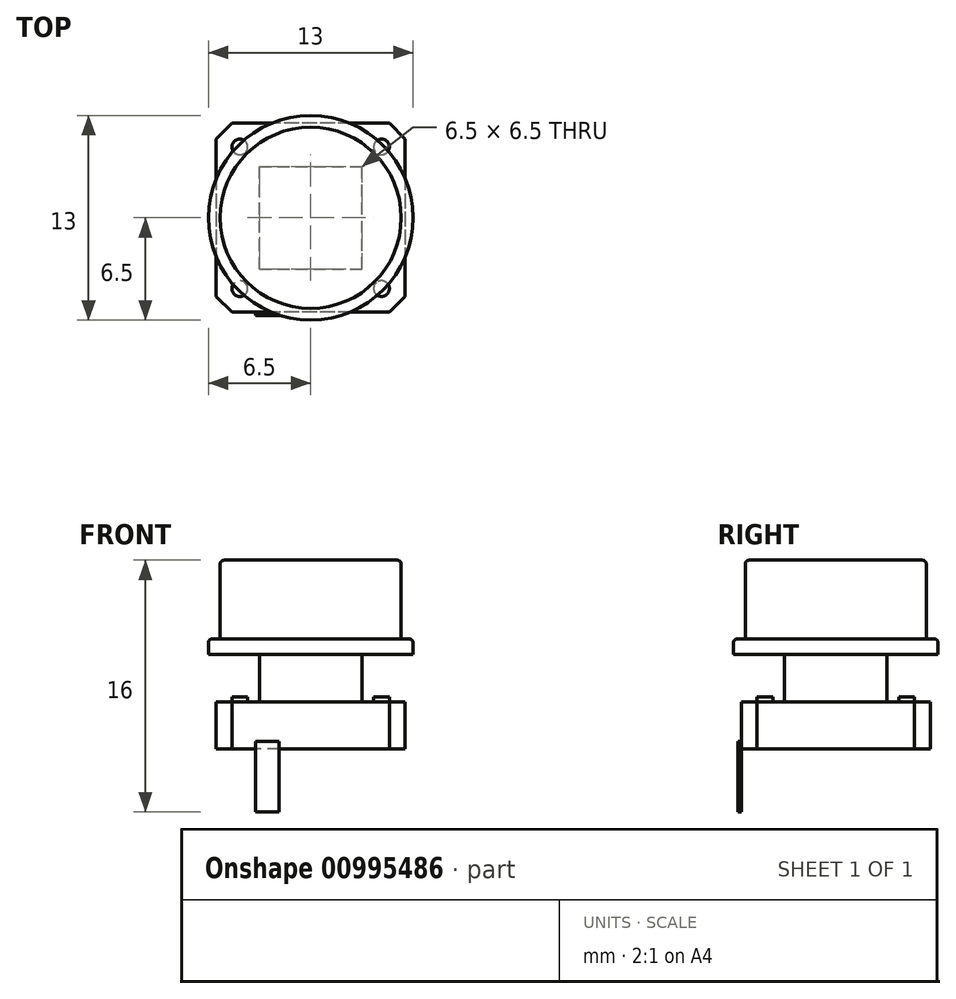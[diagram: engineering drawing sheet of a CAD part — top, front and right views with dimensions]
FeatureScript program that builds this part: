
annotation { "Feature Type Name" : "Feature", "Feature Type Description" : "" }
export const myFeature = defineFeature(function(context is Context, id is Id, definition is map)
    precondition{}
    {
        {
            var Q0;
            Q0=qCreatedBy(makeId("Top.planeOp"),FACE);
            var sketch = newSketch(context, id + "F0", { "sketchPlane" : qUnion([Q0])});
            skLineSegment(sketch, "E0.bottom", {"start": v(6, 6) * mm, "end": v(-6, 6) * mm});
            skLineSegment(sketch, "E0.top", {"start": v(6, -6) * mm, "end": v(-6, -6) * mm});
            skLineSegment(sketch, "E0.left", {"start": v(6, 6) * mm, "end": v(6, -6) * mm});
            skLineSegment(sketch, "E0.right", {"start": v(-6, 6) * mm, "end": v(-6, -6) * mm});
            skPoint(sketch, "E0.middle", {"position": v(0, 0) * mm});
            skCircle(sketch, "E1", {"center": v(0, 0) * mm, "radius": 5.75 * mm});
            skCircle(sketch, "E2", {"center": v(0, 0) * mm, "radius": 6.5 * mm});
            skLineSegment(sketch, "E3.bottom", {"start": v(3.25, 3.25) * mm, "end": v(-3.25, 3.25) * mm});
            skLineSegment(sketch, "E3.top", {"start": v(3.25, -3.25) * mm, "end": v(-3.25, -3.25) * mm});
            skLineSegment(sketch, "E3.left", {"start": v(3.25, 3.25) * mm, "end": v(3.25, -3.25) * mm});
            skLineSegment(sketch, "E3.right", {"start": v(-3.25, 3.25) * mm, "end": v(-3.25, -3.25) * mm});
            skLineSegment(sketch, "E4", {"start": v(6, -6) * mm, "end": v(4.5, -6) * mm});
            skLineSegment(sketch, "E5", {"start": v(4.5, -6) * mm, "end": v(4.5, -4.5) * mm});
            skCircle(sketch, "E6", {"center": v(4.5, -4.5) * mm, "radius": 0.5 * mm});
            skCircle(sketch, "E7.MirrorC", {"center": v(-4.5, -4.5) * mm, "radius": 0.5 * mm});
            skCircle(sketch, "E8.MirrorC", {"center": v(-4.5, 4.5) * mm, "radius": 0.5 * mm});
            skCircle(sketch, "E9.MirrorC", {"center": v(4.5, 4.5) * mm, "radius": 0.5 * mm});
            skSolve(sketch);
        }
        {
            var Q0;
            {var subQ0=sQuery(id+"F0.wireOp",EDGE,"E0.right");var subQ1=sQuery(id+"F0.wireOp",EDGE,"E0.bottom");var subQ2=makeQuery(id+"F0.imprint","INTERSECT",VERTEX,{"derivedFrom":[subQ1,subQ0]});Q0=makeQuery(id+"F0.imprint","IMPRINT",FACE,{"disambiguationData":[TD([[makeQuery(id+"F0.imprint","IMPRINT",EDGE,{"disambiguationData":[TD([[subQ2,1.0]])],"derivedFrom":subQ1}),1.0]])]});}
            var Q1;
            Q1=makeQuery(id+"F0.imprint","IMPRINT",FACE,{"disambiguationData":[TD([[makeQuery(id+"F0.imprint","IMPRINT",EDGE,{"derivedFrom":sQuery(id+"F0.wireOp",EDGE,"E1")}),1.0]])]});
            var Q2;
            Q2=makeQuery(id+"F0.imprint","IMPRINT",FACE,{"disambiguationData":[TD([[makeQuery(id+"F0.imprint","IMPRINT",EDGE,{"derivedFrom":sQuery(id+"F0.wireOp",EDGE,"E3.bottom")}),1.0]])]});
            var Q3;
            {var subQ0=sQuery(id+"F0.wireOp",EDGE,"E0.left");var subQ1=sQuery(id+"F0.wireOp",EDGE,"E0.bottom");var subQ2=makeQuery(id+"F0.imprint","INTERSECT",VERTEX,{"derivedFrom":[subQ1,subQ0]});Q3=makeQuery(id+"F0.imprint","IMPRINT",FACE,{"disambiguationData":[TD([[makeQuery(id+"F0.imprint","IMPRINT",EDGE,{"disambiguationData":[TD([[subQ2,-1.0]])],"derivedFrom":subQ1}),1.0]])]});}
            var Q4;
            {var subQ0=sQuery(id+"F0.wireOp",EDGE,"E0.left");var subQ1=sQuery(id+"F0.wireOp",EDGE,"E0.top");var subQ2=makeQuery(id+"F0.imprint","INTERSECT",VERTEX,{"derivedFrom":[subQ1,subQ0]});Q4=makeQuery(id+"F0.imprint","IMPRINT",FACE,{"disambiguationData":[TD([[makeQuery(id+"F0.imprint","IMPRINT",EDGE,{"disambiguationData":[TD([[subQ2,-1.0]])],"derivedFrom":subQ1}),-1.0]])]});}
            var Q5;
            {var subQ0=sQuery(id+"F0.wireOp",EDGE,"E0.right");var subQ1=sQuery(id+"F0.wireOp",EDGE,"E0.top");var subQ2=makeQuery(id+"F0.imprint","INTERSECT",VERTEX,{"derivedFrom":[subQ1,subQ0]});Q5=makeQuery(id+"F0.imprint","IMPRINT",FACE,{"disambiguationData":[TD([[makeQuery(id+"F0.imprint","IMPRINT",EDGE,{"disambiguationData":[TD([[subQ2,1.0]])],"derivedFrom":subQ1}),-1.0]])]});}
            var Q6;
            Q6=makeQuery(id+"F0.imprint","IMPRINT",FACE,{"disambiguationData":[TD([[makeQuery(id+"F0.imprint","IMPRINT",EDGE,{"derivedFrom":sQuery(id+"F0.wireOp",EDGE,"E1")}),-1.0]])]});
            var Q7;
            {var subQ0=sQuery(id+"F0.wireOp",EDGE,"E9.MirrorC");var subQ1=sQuery(id+"F0.wireOp",EDGE,"E2");var subQ2=makeQuery(id+"F0.imprint","INTERSECT",VERTEX,{"disambiguationData":[OD(0.0)],"derivedFrom":[subQ1,subQ0]});Q7=makeQuery(id+"F0.imprint","IMPRINT",FACE,{"disambiguationData":[TD([[makeQuery(id+"F0.imprint","IMPRINT",EDGE,{"disambiguationData":[TD([[subQ2,-1.0]])],"derivedFrom":subQ1}),-1.0]])]});}
            var Q8;
            {var subQ0=sQuery(id+"F0.wireOp",EDGE,"E9.MirrorC");var subQ1=sQuery(id+"F0.wireOp",EDGE,"E2");var subQ2=makeQuery(id+"F0.imprint","INTERSECT",VERTEX,{"disambiguationData":[OD(0.0)],"derivedFrom":[subQ1,subQ0]});Q8=makeQuery(id+"F0.imprint","IMPRINT",FACE,{"disambiguationData":[TD([[makeQuery(id+"F0.imprint","IMPRINT",EDGE,{"disambiguationData":[TD([[subQ2,-1.0]])],"derivedFrom":subQ1}),1.0]])]});}
            var Q9;
            {var subQ0=sQuery(id+"F0.wireOp",EDGE,"E8.MirrorC");var subQ1=sQuery(id+"F0.wireOp",EDGE,"E2");var subQ2=makeQuery(id+"F0.imprint","INTERSECT",VERTEX,{"disambiguationData":[OD(0.0)],"derivedFrom":[subQ1,subQ0]});Q9=makeQuery(id+"F0.imprint","IMPRINT",FACE,{"disambiguationData":[TD([[makeQuery(id+"F0.imprint","IMPRINT",EDGE,{"disambiguationData":[TD([[subQ2,-1.0]])],"derivedFrom":subQ1}),-1.0]])]});}
            var Q10;
            {var subQ0=sQuery(id+"F0.wireOp",EDGE,"E8.MirrorC");var subQ1=sQuery(id+"F0.wireOp",EDGE,"E2");var subQ2=makeQuery(id+"F0.imprint","INTERSECT",VERTEX,{"disambiguationData":[OD(0.0)],"derivedFrom":[subQ1,subQ0]});Q10=makeQuery(id+"F0.imprint","IMPRINT",FACE,{"disambiguationData":[TD([[makeQuery(id+"F0.imprint","IMPRINT",EDGE,{"disambiguationData":[TD([[subQ2,-1.0]])],"derivedFrom":subQ1}),1.0]])]});}
            var Q11;
            {var subQ0=sQuery(id+"F0.wireOp",EDGE,"E7.MirrorC");var subQ1=sQuery(id+"F0.wireOp",EDGE,"E2");var subQ2=makeQuery(id+"F0.imprint","INTERSECT",VERTEX,{"disambiguationData":[OD(0.0)],"derivedFrom":[subQ1,subQ0]});Q11=makeQuery(id+"F0.imprint","IMPRINT",FACE,{"disambiguationData":[TD([[makeQuery(id+"F0.imprint","IMPRINT",EDGE,{"disambiguationData":[TD([[subQ2,-1.0]])],"derivedFrom":subQ1}),-1.0]])]});}
            var Q12;
            {var subQ0=sQuery(id+"F0.wireOp",EDGE,"E7.MirrorC");var subQ1=sQuery(id+"F0.wireOp",EDGE,"E2");var subQ2=makeQuery(id+"F0.imprint","INTERSECT",VERTEX,{"disambiguationData":[OD(0.0)],"derivedFrom":[subQ1,subQ0]});Q12=makeQuery(id+"F0.imprint","IMPRINT",FACE,{"disambiguationData":[TD([[makeQuery(id+"F0.imprint","IMPRINT",EDGE,{"disambiguationData":[TD([[subQ2,-1.0]])],"derivedFrom":subQ1}),1.0]])]});}
            var Q13;
            {var subQ1=sQuery(id+"F0.wireOp",EDGE,"E4");Q13=makeQuery(id+"F0.imprint","IMPRINT",FACE,{"disambiguationData":[TD([[makeQuery(id+"F0.imprint","IMPRINT",EDGE,{"derivedFrom":subQ1}),-1.0]])]});}
            var Q14;
            {var subQ1=sQuery(id+"F0.wireOp",EDGE,"E0.top");var subQ3=sQuery(id+"F0.wireOp",EDGE,"E2");var subQ4=makeQuery(id+"F0.imprint","INTERSECT",VERTEX,{"disambiguationData":[OD(0.0)],"derivedFrom":[subQ1,subQ3]});Q14=makeQuery(id+"F0.imprint","IMPRINT",FACE,{"disambiguationData":[TD([[makeQuery(id+"F0.imprint","IMPRINT",EDGE,{"disambiguationData":[TD([[subQ4,-1.0]])],"derivedFrom":subQ3}),-1.0]])]});}
            var Q15;
            {var subQ0=sQuery(id+"F0.wireOp",EDGE,"E5");var subQ1=sQuery(id+"F0.wireOp",EDGE,"E2");var subQ2=makeQuery(id+"F0.imprint","INTERSECT",VERTEX,{"derivedFrom":[subQ1,subQ0]});Q15=makeQuery(id+"F0.imprint","IMPRINT",FACE,{"disambiguationData":[TD([[makeQuery(id+"F0.imprint","IMPRINT",EDGE,{"disambiguationData":[TD([[subQ2,-1.0]])],"derivedFrom":subQ1}),-1.0]])]});}
            var Q16;
            {var subQ0=sQuery(id+"F0.wireOp",EDGE,"E2");var subQ1=makeQuery(id+"F0.imprint","INTERSECT",VERTEX,{"derivedFrom":[subQ0,sQuery(id+"F0.wireOp",EDGE,"E5")]});Q16=makeQuery(id+"F0.imprint","IMPRINT",FACE,{"disambiguationData":[TD([[makeQuery(id+"F0.imprint","IMPRINT",EDGE,{"disambiguationData":[TD([[subQ1,1.0]])],"derivedFrom":subQ0}),1.0]])]});}
            var Q17;
            {var subQ0=sQuery(id+"F0.wireOp",EDGE,"E5");var subQ1=sQuery(id+"F0.wireOp",EDGE,"E2");var subQ2=makeQuery(id+"F0.imprint","INTERSECT",VERTEX,{"derivedFrom":[subQ1,subQ0]});Q17=makeQuery(id+"F0.imprint","IMPRINT",FACE,{"disambiguationData":[TD([[makeQuery(id+"F0.imprint","IMPRINT",EDGE,{"disambiguationData":[TD([[subQ2,1.0]])],"derivedFrom":subQ1}),-1.0]])]});}
            extrude(context, id + "F1", {"entities" : qUnion([Q0, Q1, Q2, Q3, Q4, Q5, Q6, Q7, Q8, Q9, Q10, Q11, Q12, Q13, Q14, Q15, Q16, Q17]), "depth" : 3 * mm, "offsetDistance" : 25 * mm});
        }
        {
            var Q0;
            Q0=makeQuery(id+"F0.imprint","IMPRINT",FACE,{"disambiguationData":[TD([[makeQuery(id+"F0.imprint","IMPRINT",EDGE,{"derivedFrom":sQuery(id+"F0.wireOp",EDGE,"E3.bottom")}),1.0]])]});
            extrude(context, id + "F2", {"entities" : qUnion([Q0]), "operationType" : NewBodyOperationType.ADD, "depth" : 6 * mm, "offsetDistance" : 25 * mm});
        }
        {
            var Q0;
            Q0=makeQuery(id+"F0.imprint","IMPRINT",FACE,{"disambiguationData":[TD([[makeQuery(id+"F0.imprint","IMPRINT",EDGE,{"derivedFrom":sQuery(id+"F0.wireOp",EDGE,"E1")}),1.0]])]});
            var Q1;
            Q1=makeQuery(id+"F0.imprint","IMPRINT",FACE,{"disambiguationData":[TD([[makeQuery(id+"F0.imprint","IMPRINT",EDGE,{"derivedFrom":sQuery(id+"F0.wireOp",EDGE,"E3.bottom")}),1.0]])]});
            extrude(context, id + "F3", {"entities" : qUnion([Q0, Q1]), "operationType" : NewBodyOperationType.ADD, "depth" : 12 * mm, "offsetDistance" : 25 * mm, "hasSecondDirection" : true, "secondDirectionOppositeDirection" : false, "secondDirectionDepth" : 6 * mm});
        }
        {
            var Q0;
            Q0=makeQuery(id+"F0.imprint","IMPRINT",FACE,{"disambiguationData":[TD([[makeQuery(id+"F0.imprint","IMPRINT",EDGE,{"derivedFrom":sQuery(id+"F0.wireOp",EDGE,"E1")}),-1.0]])]});
            var Q1;
            {var subQ0=sQuery(id+"F0.wireOp",EDGE,"E2");var subQ1=sQuery(id+"F0.wireOp",EDGE,"E0.bottom");var subQ2=makeQuery(id+"F0.imprint","INTERSECT",VERTEX,{"disambiguationData":[OD(0.0)],"derivedFrom":[subQ1,subQ0]});Q1=makeQuery(id+"F0.imprint","IMPRINT",FACE,{"disambiguationData":[TD([[makeQuery(id+"F0.imprint","IMPRINT",EDGE,{"disambiguationData":[TD([[subQ2,-1.0]])],"derivedFrom":subQ1}),-1.0]])]});}
            var Q2;
            {var subQ0=sQuery(id+"F0.wireOp",EDGE,"E2");var subQ1=sQuery(id+"F0.wireOp",EDGE,"E0.left");var subQ2=makeQuery(id+"F0.imprint","INTERSECT",VERTEX,{"disambiguationData":[OD(0.0)],"derivedFrom":[subQ1,subQ0]});Q2=makeQuery(id+"F0.imprint","IMPRINT",FACE,{"disambiguationData":[TD([[makeQuery(id+"F0.imprint","IMPRINT",EDGE,{"disambiguationData":[TD([[subQ2,-1.0]])],"derivedFrom":subQ1}),1.0]])]});}
            var Q3;
            {var subQ0=sQuery(id+"F0.wireOp",EDGE,"E2");var subQ1=sQuery(id+"F0.wireOp",EDGE,"E0.top");var subQ2=makeQuery(id+"F0.imprint","INTERSECT",VERTEX,{"disambiguationData":[OD(0.0)],"derivedFrom":[subQ1,subQ0]});Q3=makeQuery(id+"F0.imprint","IMPRINT",FACE,{"disambiguationData":[TD([[makeQuery(id+"F0.imprint","IMPRINT",EDGE,{"disambiguationData":[TD([[subQ2,-1.0]])],"derivedFrom":subQ1}),1.0]])]});}
            var Q4;
            {var subQ0=sQuery(id+"F0.wireOp",EDGE,"E2");var subQ1=sQuery(id+"F0.wireOp",EDGE,"E0.right");var subQ2=makeQuery(id+"F0.imprint","INTERSECT",VERTEX,{"disambiguationData":[OD(0.0)],"derivedFrom":[subQ1,subQ0]});Q4=makeQuery(id+"F0.imprint","IMPRINT",FACE,{"disambiguationData":[TD([[makeQuery(id+"F0.imprint","IMPRINT",EDGE,{"disambiguationData":[TD([[subQ2,-1.0]])],"derivedFrom":subQ1}),-1.0]])]});}
            var Q5;
            {var subQ0=sQuery(id+"F0.wireOp",EDGE,"E2");var subQ1=makeQuery(id+"F0.imprint","INTERSECT",VERTEX,{"derivedFrom":[subQ0,sQuery(id+"F0.wireOp",EDGE,"E5")]});Q5=makeQuery(id+"F0.imprint","IMPRINT",FACE,{"disambiguationData":[TD([[makeQuery(id+"F0.imprint","IMPRINT",EDGE,{"disambiguationData":[TD([[subQ1,1.0]])],"derivedFrom":subQ0}),1.0]])]});}
            var Q6;
            {var subQ0=sQuery(id+"F0.wireOp",EDGE,"E7.MirrorC");var subQ1=sQuery(id+"F0.wireOp",EDGE,"E2");var subQ2=makeQuery(id+"F0.imprint","INTERSECT",VERTEX,{"disambiguationData":[OD(0.0)],"derivedFrom":[subQ1,subQ0]});Q6=makeQuery(id+"F0.imprint","IMPRINT",FACE,{"disambiguationData":[TD([[makeQuery(id+"F0.imprint","IMPRINT",EDGE,{"disambiguationData":[TD([[subQ2,-1.0]])],"derivedFrom":subQ1}),1.0]])]});}
            var Q7;
            {var subQ0=sQuery(id+"F0.wireOp",EDGE,"E8.MirrorC");var subQ1=sQuery(id+"F0.wireOp",EDGE,"E2");var subQ2=makeQuery(id+"F0.imprint","INTERSECT",VERTEX,{"disambiguationData":[OD(0.0)],"derivedFrom":[subQ1,subQ0]});Q7=makeQuery(id+"F0.imprint","IMPRINT",FACE,{"disambiguationData":[TD([[makeQuery(id+"F0.imprint","IMPRINT",EDGE,{"disambiguationData":[TD([[subQ2,-1.0]])],"derivedFrom":subQ1}),1.0]])]});}
            var Q8;
            {var subQ0=sQuery(id+"F0.wireOp",EDGE,"E9.MirrorC");var subQ1=sQuery(id+"F0.wireOp",EDGE,"E2");var subQ2=makeQuery(id+"F0.imprint","INTERSECT",VERTEX,{"disambiguationData":[OD(0.0)],"derivedFrom":[subQ1,subQ0]});Q8=makeQuery(id+"F0.imprint","IMPRINT",FACE,{"disambiguationData":[TD([[makeQuery(id+"F0.imprint","IMPRINT",EDGE,{"disambiguationData":[TD([[subQ2,-1.0]])],"derivedFrom":subQ1}),1.0]])]});}
            extrude(context, id + "F4", {"entities" : qUnion([Q0, Q1, Q2, Q3, Q4, Q5, Q6, Q7, Q8]), "operationType" : NewBodyOperationType.ADD, "depth" : 7 * mm, "offsetDistance" : 25 * mm, "hasSecondDirection" : true, "secondDirectionOppositeDirection" : false, "secondDirectionDepth" : 6 * mm});
        }
        {
            var Q0;
            Q0=qCreatedBy(makeId("Top.planeOp"),FACE);
            var sketch = newSketch(context, id + "F5", { "sketchPlane" : qUnion([Q0])});
            skLineSegment(sketch, "E10", {"start": v(-6, -6) * mm, "end": v(6, -6) * mm});
            skLineSegment(sketch, "E11", {"start": v(-6, -6) * mm, "end": v(-6, 6) * mm});
            skLineSegment(sketch, "E12", {"start": v(-6, 6) * mm, "end": v(6, 6) * mm});
            skLineSegment(sketch, "E13", {"start": v(-6, 6) * mm, "end": v(-3.5, 6) * mm});
            skLineSegment(sketch, "E14", {"start": v(-3.5, 6) * mm, "end": v(-2, 6) * mm});
            skLineSegment(sketch, "E15", {"start": v(6, 6) * mm, "end": v(3.5, 6) * mm});
            skLineSegment(sketch, "E16", {"start": v(3.5, 6) * mm, "end": v(2, 6) * mm});
            skLineSegment(sketch, "E17", {"start": v(-2, 6) * mm, "end": v(2, 6) * mm});
            skLineSegment(sketch, "E18.top", {"start": v(-3.5, 6.2) * mm, "end": v(-2, 6.2) * mm});
            skLineSegment(sketch, "E18.left", {"start": v(-3.5, 6) * mm, "end": v(-3.5, 6.2) * mm});
            skLineSegment(sketch, "E18.right", {"start": v(-2, 6) * mm, "end": v(-2, 6.2) * mm});
            skLineSegment(sketch, "E19.bottom", {"start": v(2, 6) * mm, "end": v(3.5, 6) * mm});
            skLineSegment(sketch, "E19.top", {"start": v(2, 6.2) * mm, "end": v(3.5, 6.2) * mm});
            skLineSegment(sketch, "E19.left", {"start": v(2, 6) * mm, "end": v(2, 6.2) * mm});
            skLineSegment(sketch, "E19.right", {"start": v(3.5, 6) * mm, "end": v(3.5, 6.2) * mm});
            skLineSegment(sketch, "E20", {"start": v(-6, 0) * mm, "end": v(0, 0) * mm});
            skLineSegment(sketch, "E21.MirrorCS", {"start": v(-3.5, -6.2) * mm, "end": v(-2, -6.2) * mm});
            skLineSegment(sketch, "E22.MirrorCS", {"start": v(-3.5, -6) * mm, "end": v(-3.5, -6.2) * mm});
            skLineSegment(sketch, "E23.MirrorCS", {"start": v(-3.5, -6) * mm, "end": v(-2, -6) * mm});
            skLineSegment(sketch, "E24.MirrorCS", {"start": v(-2, -6) * mm, "end": v(-2, -6.2) * mm});
            skLineSegment(sketch, "E25.MirrorCS", {"start": v(3.5, -6) * mm, "end": v(2, -6) * mm});
            skLineSegment(sketch, "E26.MirrorCS", {"start": v(2, -6.2) * mm, "end": v(3.5, -6.2) * mm});
            skLineSegment(sketch, "E27.MirrorCS", {"start": v(3.5, -6) * mm, "end": v(3.5, -6.2) * mm});
            skLineSegment(sketch, "E28.MirrorCS", {"start": v(2, -6) * mm, "end": v(2, -6.2) * mm});
            skSolve(sketch);
        }
        {
            var Q0;
            Q0=makeQuery(id+"F5.imprint","IMPRINT",FACE,{"disambiguationData":[TD([[makeQuery(id+"F5.imprint","IMPRINT",EDGE,{"derivedFrom":sQuery(id+"F5.wireOp",EDGE,"E21.MirrorCS")}),1.0]])]});
            var Q1;
            Q1=makeQuery(id+"F5.imprint","IMPRINT",FACE,{"disambiguationData":[TD([[makeQuery(id+"F5.imprint","IMPRINT",EDGE,{"derivedFrom":sQuery(id+"F5.wireOp",EDGE,"E25.MirrorCS")}),1.0]])]});
            var Q2;
            Q2=makeQuery(id+"F5.imprint","IMPRINT",FACE,{"disambiguationData":[TD([[makeQuery(id+"F5.imprint","IMPRINT",EDGE,{"derivedFrom":sQuery(id+"F5.wireOp",EDGE,"E19.bottom")}),1.0]])]});
            var Q3;
            Q3=makeQuery(id+"F5.imprint","IMPRINT",FACE,{"disambiguationData":[TD([[makeQuery(id+"F5.imprint","IMPRINT",EDGE,{"derivedFrom":sQuery(id+"F5.wireOp",EDGE,"E14")}),1.0]])]});
            extrude(context, id + "F6", {"entities" : qUnion([Q0, Q1, Q2, Q3]), "operationType" : NewBodyOperationType.ADD, "oppositeDirection" : true, "depth" : 4 * mm, "offsetDistance" : 25 * mm, "hasSecondDirection" : true, "secondDirectionOppositeDirection" : false, "secondDirectionDepth" : 0.5 * mm});
        }
        {
            var Q0;
            Q0=makeQuery(id+"F1.opExtrude","SWEPT_EDGE",EDGE,{"disambiguationData":[OSD([sQuery(id+"F0.wireOp",EDGE,"E0.top"),sQuery(id+"F0.wireOp",EDGE,"E0.right")])]});
            var Q1;
            Q1=makeQuery(id+"F1.opExtrude","SWEPT_EDGE",EDGE,{"disambiguationData":[OSD([sQuery(id+"F0.wireOp",EDGE,"E0.top"),sQuery(id+"F0.wireOp",EDGE,"E0.left")])]});
            var Q2;
            Q2=makeQuery(id+"F1.opExtrude","SWEPT_EDGE",EDGE,{"disambiguationData":[OSD([sQuery(id+"F0.wireOp",EDGE,"E0.bottom"),sQuery(id+"F0.wireOp",EDGE,"E0.left")])]});
            var Q3;
            Q3=makeQuery(id+"F1.opExtrude","SWEPT_EDGE",EDGE,{"disambiguationData":[OSD([sQuery(id+"F0.wireOp",EDGE,"E0.bottom"),sQuery(id+"F0.wireOp",EDGE,"E0.right")])]});
            chamfer(context, id + "F7", {"entities" : qUnion([Q0, Q1, Q2, Q3]), "width" : 1 * mm, "tangentPropagation" : true});
        }
        {
            var Q0;
            {var subQ0=sQuery(id+"F0.wireOp",EDGE,"E2");var subQ1=makeQuery(id+"F0.imprint","INTERSECT",VERTEX,{"derivedFrom":[subQ0,sQuery(id+"F0.wireOp",EDGE,"E5")]});Q0=makeQuery(id+"F0.imprint","IMPRINT",FACE,{"disambiguationData":[TD([[makeQuery(id+"F0.imprint","IMPRINT",EDGE,{"disambiguationData":[TD([[subQ1,1.0]])],"derivedFrom":subQ0}),1.0]])]});}
            var Q1;
            {var subQ0=sQuery(id+"F0.wireOp",EDGE,"E5");var subQ1=sQuery(id+"F0.wireOp",EDGE,"E2");var subQ2=makeQuery(id+"F0.imprint","INTERSECT",VERTEX,{"derivedFrom":[subQ1,subQ0]});Q1=makeQuery(id+"F0.imprint","IMPRINT",FACE,{"disambiguationData":[TD([[makeQuery(id+"F0.imprint","IMPRINT",EDGE,{"disambiguationData":[TD([[subQ2,-1.0]])],"derivedFrom":subQ1}),-1.0]])]});}
            var Q2;
            {var subQ0=sQuery(id+"F0.wireOp",EDGE,"E5");var subQ1=sQuery(id+"F0.wireOp",EDGE,"E2");var subQ2=makeQuery(id+"F0.imprint","INTERSECT",VERTEX,{"derivedFrom":[subQ1,subQ0]});Q2=makeQuery(id+"F0.imprint","IMPRINT",FACE,{"disambiguationData":[TD([[makeQuery(id+"F0.imprint","IMPRINT",EDGE,{"disambiguationData":[TD([[subQ2,1.0]])],"derivedFrom":subQ1}),-1.0]])]});}
            var Q3;
            {var subQ0=sQuery(id+"F0.wireOp",EDGE,"E9.MirrorC");var subQ1=sQuery(id+"F0.wireOp",EDGE,"E2");var subQ2=makeQuery(id+"F0.imprint","INTERSECT",VERTEX,{"disambiguationData":[OD(0.0)],"derivedFrom":[subQ1,subQ0]});Q3=makeQuery(id+"F0.imprint","IMPRINT",FACE,{"disambiguationData":[TD([[makeQuery(id+"F0.imprint","IMPRINT",EDGE,{"disambiguationData":[TD([[subQ2,-1.0]])],"derivedFrom":subQ1}),1.0]])]});}
            var Q4;
            {var subQ0=sQuery(id+"F0.wireOp",EDGE,"E9.MirrorC");var subQ1=sQuery(id+"F0.wireOp",EDGE,"E2");var subQ2=makeQuery(id+"F0.imprint","INTERSECT",VERTEX,{"disambiguationData":[OD(0.0)],"derivedFrom":[subQ1,subQ0]});Q4=makeQuery(id+"F0.imprint","IMPRINT",FACE,{"disambiguationData":[TD([[makeQuery(id+"F0.imprint","IMPRINT",EDGE,{"disambiguationData":[TD([[subQ2,-1.0]])],"derivedFrom":subQ1}),-1.0]])]});}
            var Q5;
            {var subQ0=sQuery(id+"F0.wireOp",EDGE,"E8.MirrorC");var subQ1=sQuery(id+"F0.wireOp",EDGE,"E2");var subQ2=makeQuery(id+"F0.imprint","INTERSECT",VERTEX,{"disambiguationData":[OD(0.0)],"derivedFrom":[subQ1,subQ0]});Q5=makeQuery(id+"F0.imprint","IMPRINT",FACE,{"disambiguationData":[TD([[makeQuery(id+"F0.imprint","IMPRINT",EDGE,{"disambiguationData":[TD([[subQ2,-1.0]])],"derivedFrom":subQ1}),-1.0]])]});}
            var Q6;
            {var subQ0=sQuery(id+"F0.wireOp",EDGE,"E8.MirrorC");var subQ1=sQuery(id+"F0.wireOp",EDGE,"E2");var subQ2=makeQuery(id+"F0.imprint","INTERSECT",VERTEX,{"disambiguationData":[OD(0.0)],"derivedFrom":[subQ1,subQ0]});Q6=makeQuery(id+"F0.imprint","IMPRINT",FACE,{"disambiguationData":[TD([[makeQuery(id+"F0.imprint","IMPRINT",EDGE,{"disambiguationData":[TD([[subQ2,-1.0]])],"derivedFrom":subQ1}),1.0]])]});}
            var Q7;
            {var subQ0=sQuery(id+"F0.wireOp",EDGE,"E7.MirrorC");var subQ1=sQuery(id+"F0.wireOp",EDGE,"E2");var subQ2=makeQuery(id+"F0.imprint","INTERSECT",VERTEX,{"disambiguationData":[OD(0.0)],"derivedFrom":[subQ1,subQ0]});Q7=makeQuery(id+"F0.imprint","IMPRINT",FACE,{"disambiguationData":[TD([[makeQuery(id+"F0.imprint","IMPRINT",EDGE,{"disambiguationData":[TD([[subQ2,-1.0]])],"derivedFrom":subQ1}),1.0]])]});}
            var Q8;
            {var subQ0=sQuery(id+"F0.wireOp",EDGE,"E7.MirrorC");var subQ1=sQuery(id+"F0.wireOp",EDGE,"E2");var subQ2=makeQuery(id+"F0.imprint","INTERSECT",VERTEX,{"disambiguationData":[OD(0.0)],"derivedFrom":[subQ1,subQ0]});Q8=makeQuery(id+"F0.imprint","IMPRINT",FACE,{"disambiguationData":[TD([[makeQuery(id+"F0.imprint","IMPRINT",EDGE,{"disambiguationData":[TD([[subQ2,-1.0]])],"derivedFrom":subQ1}),-1.0]])]});}
            extrude(context, id + "F8", {"entities" : qUnion([Q0, Q1, Q2, Q3, Q4, Q5, Q6, Q7, Q8]), "operationType" : NewBodyOperationType.ADD, "depth" : 3.3 * mm, "offsetDistance" : 25 * mm});
        }
        {
            var Q0;
            Q0=makeQuery(id+"F3.opExtrude","CAP_EDGE",EDGE,{"disambiguationData":[OSD([sQuery(id+"F0.wireOp",EDGE,"E1")])],"isStart":false});
            var Q1;
            Q1=makeQuery(id+"F4.opExtrude","CAP_EDGE",EDGE,{"disambiguationData":[OSD([sQuery(id+"F0.wireOp",EDGE,"E2")])],"isStart":false});
            fillet(context, id + "F9", {"entities" : qUnion([Q0, Q1]), "radius" : 0.25 * mm, "tangentPropagation" : true, "allowEdgeOverflow" : false});
        }
    });
